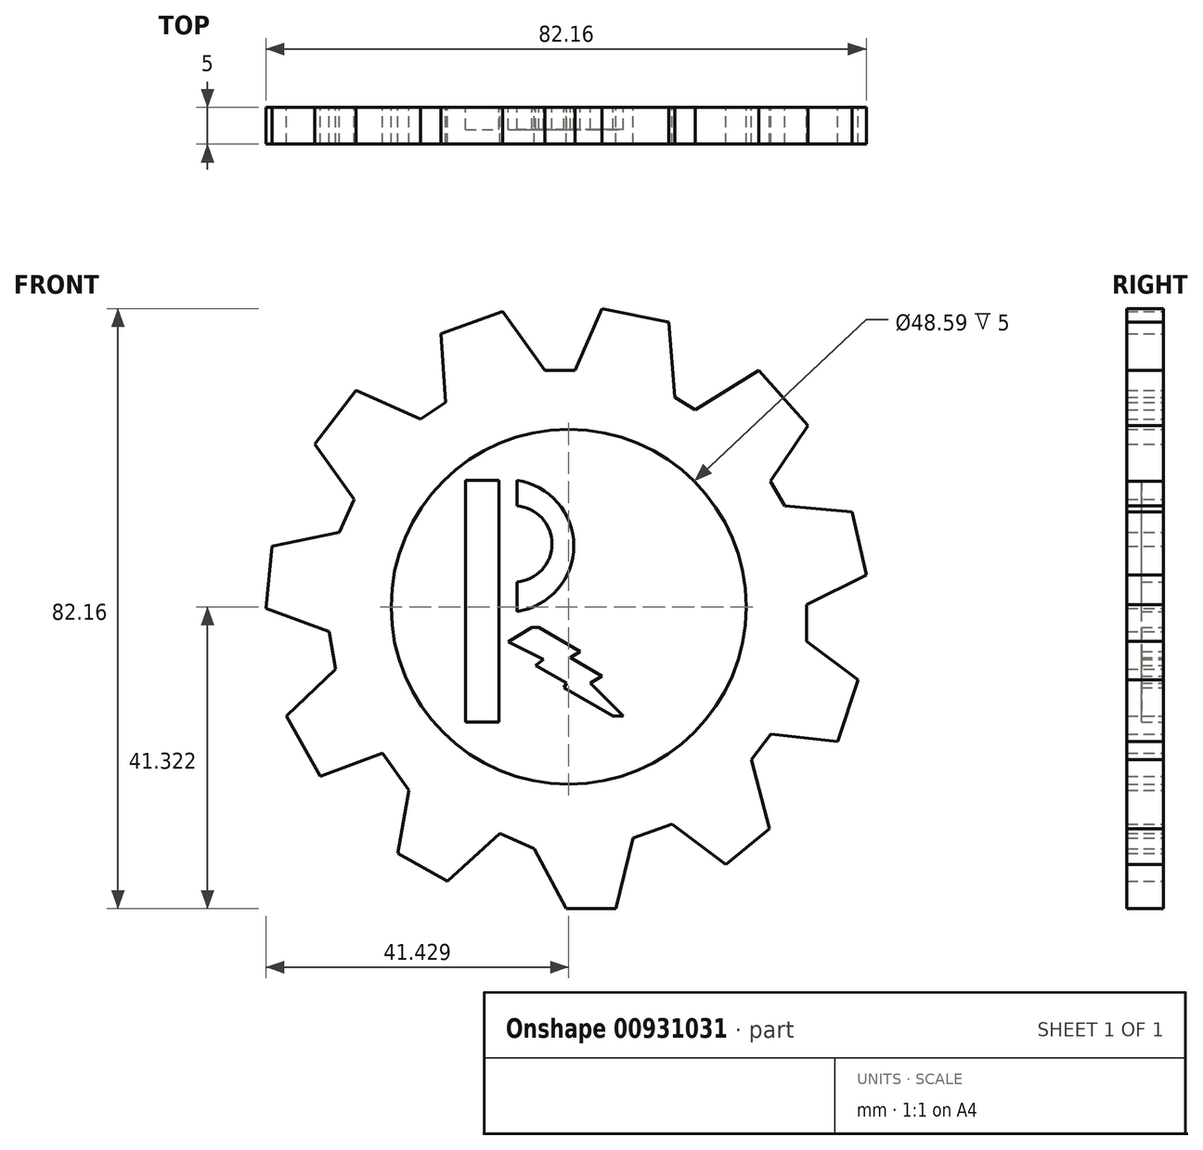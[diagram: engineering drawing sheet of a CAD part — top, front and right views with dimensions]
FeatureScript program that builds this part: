
annotation { "Feature Type Name" : "Feature", "Feature Type Description" : "" }
export const myFeature = defineFeature(function(context is Context, id is Id, definition is map)
    precondition{}
    {
        {
            var Q0;
            Q0=qCreatedBy(makeId("Front.planeOp"),FACE);
            var sketch = newSketch(context, id + "F0", { "sketchPlane" : qUnion([Q0])});
            skLineSegment(sketch, "E0", {"start": v(-29.93, 30.25) * mm, "end": v(-35.63, 22.9) * mm});
            skLineSegment(sketch, "E1", {"start": v(-41.43, 8.97) * mm, "end": v(-42.29, 0.4) * mm});
            skLineSegment(sketch, "E2", {"start": v(-41.43, 8.97) * mm, "end": v(-32.21, 10.86) * mm});
            skLineSegment(sketch, "E3", {"start": v(-32.21, 10.86) * mm, "end": v(-30.21, 15.32) * mm});
            skLineSegment(sketch, "E4", {"start": v(-30.21, 15.32) * mm, "end": v(-35.63, 22.9) * mm});
            skLineSegment(sketch, "E5", {"start": v(-42.29, 0.4) * mm, "end": v(-33.65, -2.77) * mm});
            skLineSegment(sketch, "E6", {"start": v(-33.65, -2.77) * mm, "end": v(-32.73, -7.86) * mm});
            skLineSegment(sketch, "E7", {"start": v(-29.93, 30.25) * mm, "end": v(-21.15, 26.32) * mm});
            skLineSegment(sketch, "E8", {"start": v(-21.15, 26.32) * mm, "end": v(-17.68, 28.63) * mm});
            skLineSegment(sketch, "E9", {"start": v(-17.68, 28.63) * mm, "end": v(-18.3, 38) * mm});
            skLineSegment(sketch, "E10", {"start": v(-18.3, 38) * mm, "end": v(-9.92, 41.04) * mm});
            skLineSegment(sketch, "E11", {"start": v(-9.92, 41.04) * mm, "end": v(-4.12, 33.02) * mm});
            skLineSegment(sketch, "E12", {"start": v(-4.12, 33.02) * mm, "end": v(0, 33.02) * mm});
            skLineSegment(sketch, "E13", {"start": v(0, 33.02) * mm, "end": v(3.67, 41.48) * mm});
            skLineSegment(sketch, "E14", {"start": v(3.67, 41.48) * mm, "end": v(12.83, 39.6) * mm});
            skLineSegment(sketch, "E15", {"start": v(12.83, 39.6) * mm, "end": v(13.68, 29.34) * mm});
            skLineSegment(sketch, "E16", {"start": v(13.68, 29.34) * mm, "end": v(16.49, 27.63) * mm});
            skLineSegment(sketch, "E17", {"start": v(16.49, 27.63) * mm, "end": v(25.16, 33.02) * mm});
            skLineSegment(sketch, "E18", {"start": v(25.16, 33.02) * mm, "end": v(31.87, 25.43) * mm});
            skLineSegment(sketch, "E19", {"start": v(31.87, 25.43) * mm, "end": v(26.75, 17.86) * mm});
            skLineSegment(sketch, "E20", {"start": v(26.75, 17.86) * mm, "end": v(28.7, 14.44) * mm});
            skLineSegment(sketch, "E21", {"start": v(28.7, 14.44) * mm, "end": v(37.94, 13.64) * mm});
            skLineSegment(sketch, "E22", {"start": v(37.94, 13.64) * mm, "end": v(39.87, 5) * mm});
            skLineSegment(sketch, "E23", {"start": v(39.87, 5) * mm, "end": v(31.71, 0.97) * mm});
            skLineSegment(sketch, "E24", {"start": v(31.71, 0.97) * mm, "end": v(31.71, -4.06) * mm});
            skLineSegment(sketch, "E25", {"start": v(31.71, -4.06) * mm, "end": v(38.74, -9.36) * mm});
            skLineSegment(sketch, "E26", {"start": v(38.74, -9.36) * mm, "end": v(35.99, -17.82) * mm});
            skLineSegment(sketch, "E27", {"start": v(35.99, -17.82) * mm, "end": v(26.78, -16.76) * mm});
            skLineSegment(sketch, "E28", {"start": v(26.78, -16.76) * mm, "end": v(24.14, -20.26) * mm});
            skLineSegment(sketch, "E29", {"start": v(24.14, -20.26) * mm, "end": v(26.6, -29.74) * mm});
            skLineSegment(sketch, "E30", {"start": v(26.6, -29.74) * mm, "end": v(20.67, -34.6) * mm});
            skLineSegment(sketch, "E31", {"start": v(20.67, -34.6) * mm, "end": v(13.26, -29.1) * mm});
            skLineSegment(sketch, "E32", {"start": v(13.26, -29.1) * mm, "end": v(7.96, -31) * mm});
            skLineSegment(sketch, "E33", {"start": v(7.96, -31) * mm, "end": v(5.63, -40.68) * mm});
            skLineSegment(sketch, "E34", {"start": v(5.63, -40.68) * mm, "end": v(-1.2, -40.68) * mm});
            skLineSegment(sketch, "E35", {"start": v(-1.2, -40.68) * mm, "end": v(-5.6, -32.5) * mm});
            skLineSegment(sketch, "E36", {"start": v(-5.6, -32.5) * mm, "end": v(-10.25, -30.37) * mm});
            skLineSegment(sketch, "E37", {"start": v(-10.25, -30.37) * mm, "end": v(-17.45, -36.94) * mm});
            skLineSegment(sketch, "E38", {"start": v(-17.45, -36.94) * mm, "end": v(-24.23, -33.13) * mm});
            skLineSegment(sketch, "E39", {"start": v(-24.23, -33.13) * mm, "end": v(-22.75, -24.44) * mm});
            skLineSegment(sketch, "E40", {"start": v(-22.75, -24.44) * mm, "end": v(-26.35, -19.36) * mm});
            skLineSegment(sketch, "E41", {"start": v(-26.35, -19.36) * mm, "end": v(-34.82, -22.54) * mm});
            skLineSegment(sketch, "E42", {"start": v(-34.82, -22.54) * mm, "end": v(-39.47, -14.28) * mm});
            skLineSegment(sketch, "E43", {"start": v(-39.47, -14.28) * mm, "end": v(-32.73, -7.86) * mm});
            skCircle(sketch, "E44", {"center": v(-0.86, 0.64) * mm, "radius": 24.3 * mm});
            skPoint(sketch, "E44.first.point", {"position": v(8.48, 23.07) * mm});
            skPoint(sketch, "E44.second.point", {"position": v(-10.9, -21.49) * mm});
            skPoint(sketch, "E44.third.point", {"position": v(-23.93, 8.28) * mm});
            skSolve(sketch);
        }
        {
            var Q0;
            Q0 = qSketchRegion(id + "F0", true);
            extrude(context, id + "F1", {"entities" : qUnion([Q0]), "depth" : 5 * mm, "offsetDistance" : 25.4 * mm});
        }
        {
            var Q0;
            Q0=qCreatedBy(makeId("Front.planeOp"),FACE);
            var sketch = newSketch(context, id + "F2", { "sketchPlane" : qUnion([Q0])});
            skLineSegment(sketch, "E45.bottom", {"start": v(-15, -15.15) * mm, "end": v(-10.42, -15.15) * mm});
            skLineSegment(sketch, "E45.top", {"start": v(-15, 17.96) * mm, "end": v(-10.42, 17.96) * mm});
            skLineSegment(sketch, "E45.left", {"start": v(-15, -15.15) * mm, "end": v(-15, 17.96) * mm});
            skLineSegment(sketch, "E45.right", {"start": v(-10.42, -15.15) * mm, "end": v(-10.42, 17.96) * mm});
            skArc(sketch, "E46", {"start": v(-7.95, 0) * mm, "mid": v(-0.16, 8.98) * mm, "end": v(-7.95, 17.96) * mm});
            skLineSegment(sketch, "E47", {"start": v(-7.95, 17.96) * mm, "end": v(-7.95, 14.44) * mm});
            skLineSegment(sketch, "E48", {"start": v(-7.95, 0) * mm, "end": v(-7.95, 4.05) * mm});
            skArc(sketch, "E49", {"start": v(-7.95, 4.05) * mm, "mid": v(-3.13, 9.25) * mm, "end": v(-7.95, 14.44) * mm});
            skLineSegment(sketch, "E50", {"start": v(-9.15, -4.14) * mm, "end": v(-5.91, -2.2) * mm});
            skLineSegment(sketch, "E51", {"start": v(-5.91, -2.2) * mm, "end": v(-4.96, -2.2) * mm});
            skLineSegment(sketch, "E52", {"start": v(-4.96, -2.2) * mm, "end": v(0.7, -5.47) * mm});
            skLineSegment(sketch, "E53", {"start": v(0.7, -5.47) * mm, "end": v(-0.64, -6.28) * mm});
            skLineSegment(sketch, "E54", {"start": v(-0.64, -6.28) * mm, "end": v(3.69, -8.85) * mm});
            skLineSegment(sketch, "E55", {"start": v(3.69, -8.85) * mm, "end": v(2.1, -9.8) * mm});
            skLineSegment(sketch, "E56", {"start": v(2.1, -9.8) * mm, "end": v(6.63, -14.3) * mm});
            skLineSegment(sketch, "E57", {"start": v(6.63, -14.3) * mm, "end": v(5.22, -14.3) * mm});
            skLineSegment(sketch, "E58", {"start": v(5.22, -14.3) * mm, "end": v(-1.52, -10.46) * mm});
            skLineSegment(sketch, "E59", {"start": v(-1.52, -10.46) * mm, "end": v(-1.14, -9.8) * mm});
            skLineSegment(sketch, "E60", {"start": v(-1.14, -9.8) * mm, "end": v(-5.37, -7.38) * mm});
            skLineSegment(sketch, "E61", {"start": v(-5.37, -7.38) * mm, "end": v(-4.33, -6.54) * mm});
            skLineSegment(sketch, "E62", {"start": v(-4.33, -6.54) * mm, "end": v(-9.15, -4.14) * mm});
            skSolve(sketch);
        }
        {
            var Q0;
            Q0 = qSketchRegion(id + "F2", true);
            extrude(context, id + "F3", {"entities" : qUnion([Q0]), "depth" : 3 * mm, "offsetDistance" : 25 * mm});
        }
    });
